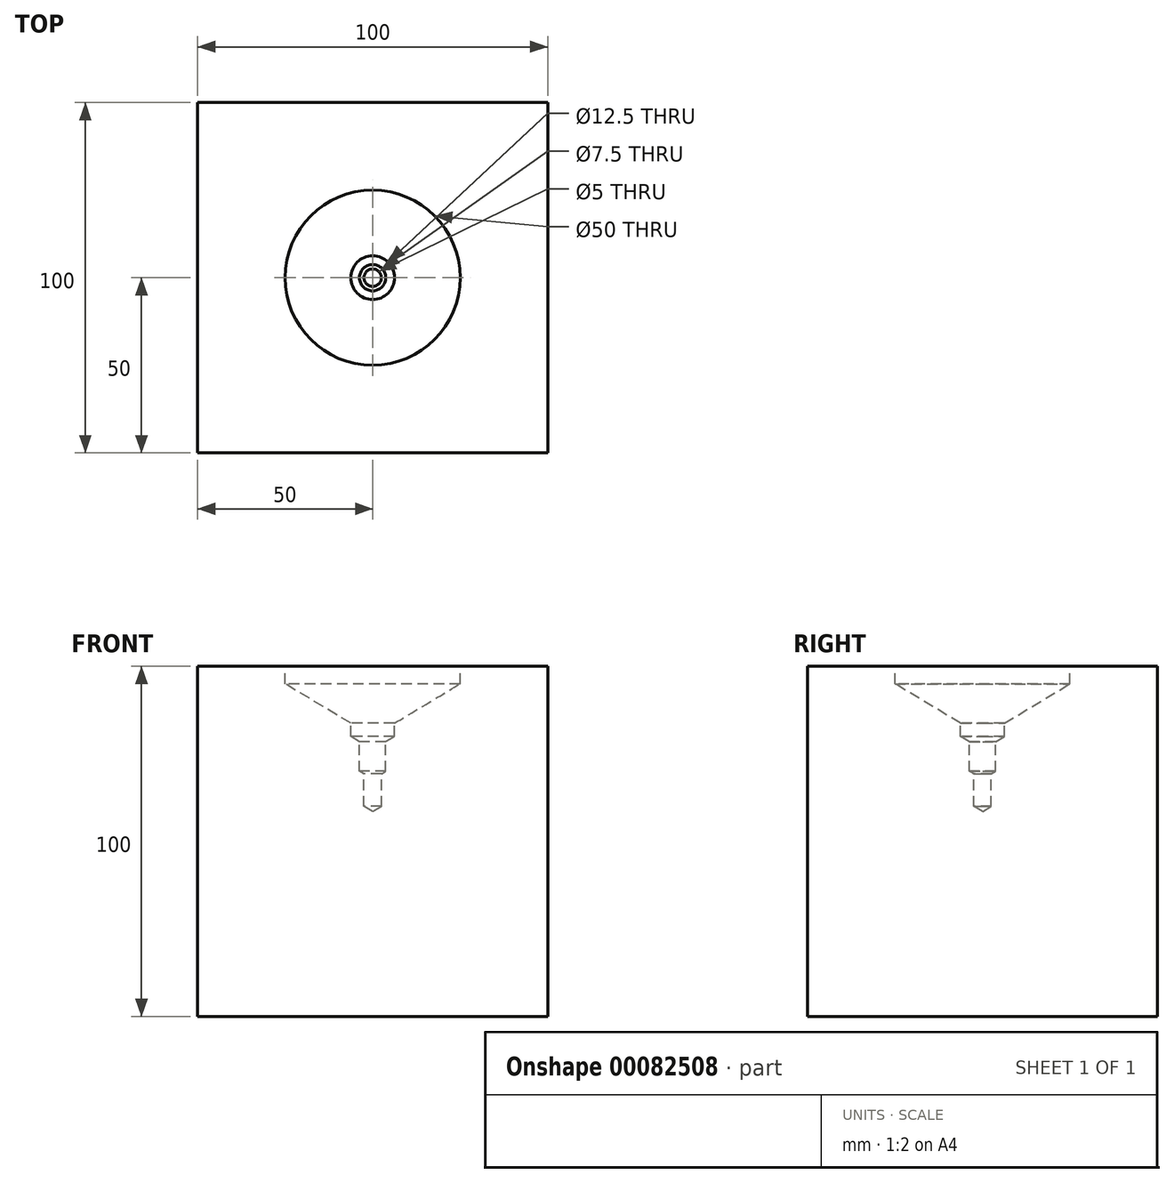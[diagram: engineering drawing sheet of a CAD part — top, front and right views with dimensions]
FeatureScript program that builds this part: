
annotation { "Feature Type Name" : "Feature", "Feature Type Description" : "" }
export const myFeature = defineFeature(function(context is Context, id is Id, definition is map)
    precondition{}
    {
        {
            var Q0;
            Q0=qCreatedBy(makeId("Front.planeOp"),FACE);
            var sketch = newSketch(context, id + "F0", { "sketchPlane" : qUnion([Q0])});
            skLineSegment(sketch, "E0.bottom", {"start": v(0, 0) * mm, "end": v(100, 0) * mm});
            skLineSegment(sketch, "E0.top", {"start": v(0, 100) * mm, "end": v(100, 100) * mm});
            skLineSegment(sketch, "E0.left", {"start": v(0, 0) * mm, "end": v(0, 100) * mm});
            skLineSegment(sketch, "E0.right", {"start": v(100, 0) * mm, "end": v(100, 100) * mm});
            skSolve(sketch);
        }
        {
            var Q0;
            Q0=qSketchRegion(id+"F0",true);
            extrude(context, id + "F1", {"entities" : qUnion([Q0]), "depth" : 100 * mm});
        }
        {
            var Q0;
            Q0=makeQuery(id+"F1.opExtrude","SWEPT_FACE",FACE,{"disambiguationData":[OSD([sQuery(id+"F0.wireOp",EDGE,"E0.top")])]});
            var sketch = newSketch(context, id + "F2", { "sketchPlane" : qUnion([Q0])});
            skPoint(sketch, "E1", {"position": v(50, -50) * mm});
            skSolve(sketch);
        }
        {
            var Q0;
            Q0=sQuery(id+"F2.wireOp",VERTEX,"E1");
            var Q1;
            Q1=makeQuery(id+"F1.opExtrude","SWEPT_BODY",BODY,{"disambiguationData":[OSD([sQuery(id+"F0.wireOp",EDGE,"E0.bottom"),sQuery(id+"F0.wireOp",EDGE,"E0.top"),sQuery(id+"F0.wireOp",EDGE,"E0.left"),sQuery(id+"F0.wireOp",EDGE,"E0.right")])]});
            hole(context, id + "F3", {"style" : HoleStyle.SIMPLE, "holeDiameter" : 5 * mm, "endStyle" : HoleEndStyle.BLIND, "holeDepth" : 40 * mm, "locations" : qUnion([Q0]), "scope" : qUnion([Q1])});
        }
        {
            var Q0;
            Q0=sQuery(id+"F2.wireOp",VERTEX,"E1");
            var Q1;
            Q1=makeQuery(id+"F1.opExtrude","SWEPT_BODY",BODY,{"disambiguationData":[OSD([sQuery(id+"F0.wireOp",EDGE,"E0.bottom"),sQuery(id+"F0.wireOp",EDGE,"E0.top"),sQuery(id+"F0.wireOp",EDGE,"E0.left"),sQuery(id+"F0.wireOp",EDGE,"E0.right")])]});
            hole(context, id + "F4", {"style" : HoleStyle.SIMPLE, "holeDiameter" : 7.5 * mm, "endStyle" : HoleEndStyle.BLIND, "holeDepth" : 30 * mm, "locations" : qUnion([Q0]), "scope" : qUnion([Q1])});
        }
        {
            var Q0;
            Q0=sQuery(id+"F2.wireOp",VERTEX,"E1");
            var Q1;
            Q1=makeQuery(id+"F1.opExtrude","SWEPT_BODY",BODY,{"disambiguationData":[OSD([sQuery(id+"F0.wireOp",EDGE,"E0.bottom"),sQuery(id+"F0.wireOp",EDGE,"E0.top"),sQuery(id+"F0.wireOp",EDGE,"E0.left"),sQuery(id+"F0.wireOp",EDGE,"E0.right")])]});
            hole(context, id + "F5", {"style" : HoleStyle.SIMPLE, "holeDiameter" : 12.5 * mm, "endStyle" : HoleEndStyle.BLIND, "holeDepth" : 20 * mm, "locations" : qUnion([Q0]), "scope" : qUnion([Q1])});
        }
        {
            var Q0;
            Q0=sQuery(id+"F2.wireOp",VERTEX,"E1");
            var Q1;
            Q1=makeQuery(id+"F1.opExtrude","SWEPT_BODY",BODY,{"disambiguationData":[OSD([sQuery(id+"F0.wireOp",EDGE,"E0.bottom"),sQuery(id+"F0.wireOp",EDGE,"E0.top"),sQuery(id+"F0.wireOp",EDGE,"E0.left"),sQuery(id+"F0.wireOp",EDGE,"E0.right")])]});
            hole(context, id + "F6", {"style" : HoleStyle.SIMPLE, "holeDiameter" : 15 * mm, "endStyle" : HoleEndStyle.BLIND, "holeDepth" : 10 * mm, "locations" : qUnion([Q0]), "scope" : qUnion([Q1])});
        }
        {
            var Q0;
            Q0=sQuery(id+"F2.wireOp",VERTEX,"E1");
            var Q1;
            Q1=makeQuery(id+"F1.opExtrude","SWEPT_BODY",BODY,{"disambiguationData":[OSD([sQuery(id+"F0.wireOp",EDGE,"E0.bottom"),sQuery(id+"F0.wireOp",EDGE,"E0.top"),sQuery(id+"F0.wireOp",EDGE,"E0.left"),sQuery(id+"F0.wireOp",EDGE,"E0.right")])]});
            hole(context, id + "F7", {"style" : HoleStyle.SIMPLE, "holeDiameter" : 30 * mm, "endStyle" : HoleEndStyle.BLIND, "holeDepth" : 5 * mm, "locations" : qUnion([Q0]), "scope" : qUnion([Q1])});
        }
        {
            var Q0;
            Q0=sQuery(id+"F2.wireOp",VERTEX,"E1");
            var Q1;
            Q1=makeQuery(id+"F1.opExtrude","SWEPT_BODY",BODY,{"disambiguationData":[OSD([sQuery(id+"F0.wireOp",EDGE,"E0.bottom"),sQuery(id+"F0.wireOp",EDGE,"E0.top"),sQuery(id+"F0.wireOp",EDGE,"E0.left"),sQuery(id+"F0.wireOp",EDGE,"E0.right")])]});
            hole(context, id + "F8", {"style" : HoleStyle.SIMPLE, "holeDiameter" : 50 * mm, "endStyle" : HoleEndStyle.BLIND, "holeDepth" : 5 * mm, "locations" : qUnion([Q0]), "scope" : qUnion([Q1])});
        }
    });
